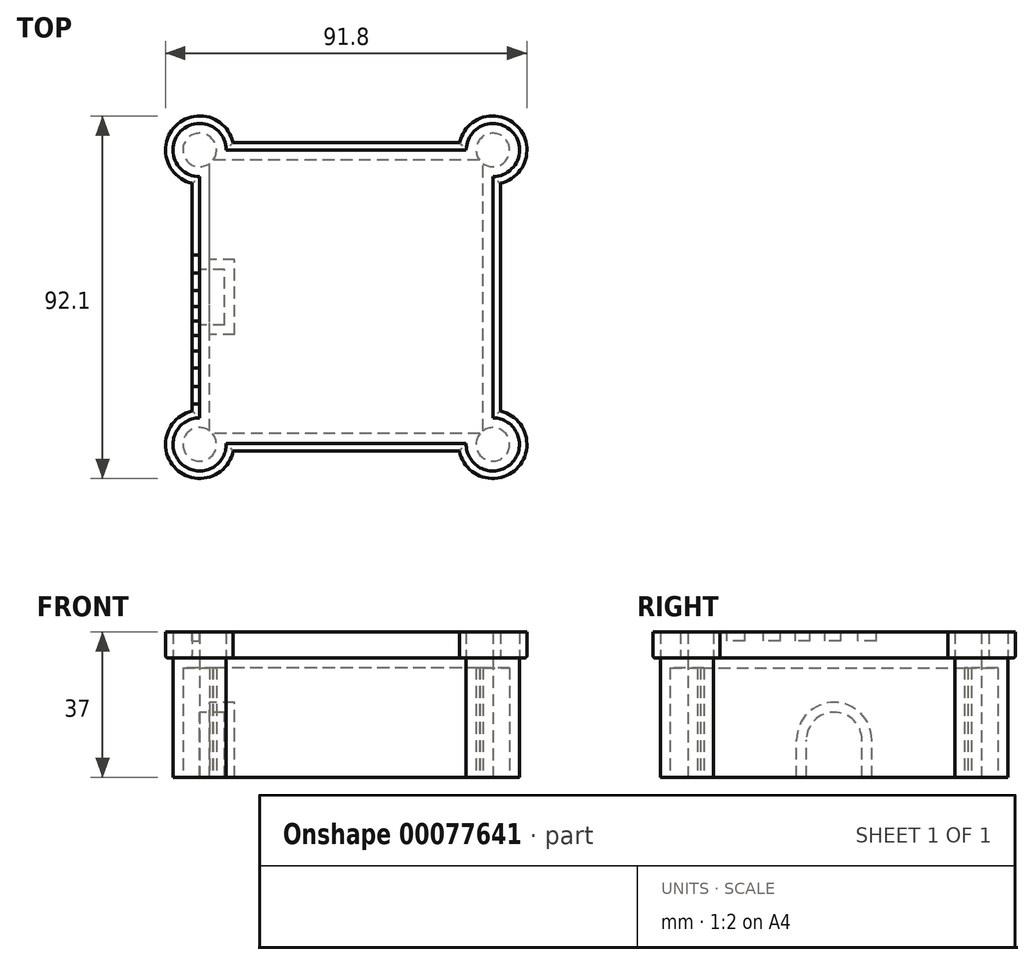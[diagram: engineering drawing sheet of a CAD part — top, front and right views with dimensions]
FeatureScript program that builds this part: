
annotation { "Feature Type Name" : "Feature", "Feature Type Description" : "" }
export const myFeature = defineFeature(function(context is Context, id is Id, definition is map)
    precondition{}
    {
        {
            var Q0;
            Q0=qCreatedBy(makeId("Top.planeOp"),FACE);
            var sketch = newSketch(context, id + "F0", { "sketchPlane" : qUnion([Q0])});
            skLineSegment(sketch, "E0.bottom", {"start": v(37.24, -37.17) * mm, "end": v(-37.24, -37.17) * mm});
            skLineSegment(sketch, "E0.top", {"start": v(37.24, 37.4) * mm, "end": v(-37.24, 37.4) * mm});
            skLineSegment(sketch, "E0.left", {"start": v(37.24, -37.17) * mm, "end": v(37.24, 37.4) * mm});
            skLineSegment(sketch, "E0.right", {"start": v(-37.24, -37.17) * mm, "end": v(-37.24, 37.4) * mm});
            skPoint(sketch, "E0.middle", {"position": v(0, 0.12) * mm});
            skCircle(sketch, "E1", {"center": v(37.24, 37.4) * mm, "radius": 6.76 * mm});
            skCircle(sketch, "E2.MirrorC", {"center": v(37.24, -37.4) * mm, "radius": 6.76 * mm});
            skCircle(sketch, "E3.MirrorC", {"center": v(-37.24, 37.4) * mm, "radius": 6.76 * mm});
            skCircle(sketch, "E4.MirrorC", {"center": v(-37.24, -37.4) * mm, "radius": 6.76 * mm});
            skSolve(sketch);
        }
        {
            var Q0;
            {var subQ5=sQuery(id+"F0.wireOp",EDGE,"E2.MirrorC");var subQ10=sQuery(id+"F0.wireOp",EDGE,"E0.bottom");var subQ11=makeQuery(id+"F0.imprint","INTERSECT",VERTEX,{"derivedFrom":[subQ10,subQ5]});Q0=makeQuery(id+"F0.imprint","IMPRINT",FACE,{"disambiguationData":[TD([[makeQuery(id+"F0.imprint","IMPRINT",EDGE,{"disambiguationData":[TD([[subQ11,-1.0]])],"derivedFrom":subQ10}),-1.0]])]});}
            var Q1;
            {var subQ0=sQuery(id+"F0.wireOp",EDGE,"E0.left");var subQ1=sQuery(id+"F0.wireOp",EDGE,"E0.bottom");var subQ2=makeQuery(id+"F0.imprint","INTERSECT",VERTEX,{"derivedFrom":[subQ1,subQ0]});Q1=makeQuery(id+"F0.imprint","IMPRINT",FACE,{"disambiguationData":[TD([[makeQuery(id+"F0.imprint","IMPRINT",EDGE,{"disambiguationData":[TD([[subQ2,-1.0]])],"derivedFrom":subQ1}),1.0]])]});}
            var Q2;
            {var subQ0=sQuery(id+"F0.wireOp",EDGE,"E0.left");var subQ1=sQuery(id+"F0.wireOp",EDGE,"E0.top");var subQ2=makeQuery(id+"F0.imprint","INTERSECT",VERTEX,{"derivedFrom":[subQ1,subQ0]});Q2=makeQuery(id+"F0.imprint","IMPRINT",FACE,{"disambiguationData":[TD([[makeQuery(id+"F0.imprint","IMPRINT",EDGE,{"disambiguationData":[TD([[subQ2,-1.0]])],"derivedFrom":subQ1}),-1.0]])]});}
            var Q3;
            {var subQ0=sQuery(id+"F0.wireOp",EDGE,"E0.right");var subQ1=sQuery(id+"F0.wireOp",EDGE,"E0.top");var subQ2=makeQuery(id+"F0.imprint","INTERSECT",VERTEX,{"derivedFrom":[subQ1,subQ0]});Q3=makeQuery(id+"F0.imprint","IMPRINT",FACE,{"disambiguationData":[TD([[makeQuery(id+"F0.imprint","IMPRINT",EDGE,{"disambiguationData":[TD([[subQ2,1.0]])],"derivedFrom":subQ1}),-1.0]])]});}
            var Q4;
            {var subQ0=sQuery(id+"F0.wireOp",EDGE,"E0.right");var subQ1=sQuery(id+"F0.wireOp",EDGE,"E0.bottom");var subQ2=makeQuery(id+"F0.imprint","INTERSECT",VERTEX,{"derivedFrom":[subQ1,subQ0]});Q4=makeQuery(id+"F0.imprint","IMPRINT",FACE,{"disambiguationData":[TD([[makeQuery(id+"F0.imprint","IMPRINT",EDGE,{"disambiguationData":[TD([[subQ2,1.0]])],"derivedFrom":subQ1}),1.0]])]});}
            var Q5;
            {var subQ0=sQuery(id+"F0.wireOp",EDGE,"E0.right");var subQ1=sQuery(id+"F0.wireOp",EDGE,"E0.bottom");var subQ2=makeQuery(id+"F0.imprint","INTERSECT",VERTEX,{"derivedFrom":[subQ1,subQ0]});Q5=makeQuery(id+"F0.imprint","IMPRINT",FACE,{"disambiguationData":[TD([[makeQuery(id+"F0.imprint","IMPRINT",EDGE,{"disambiguationData":[TD([[subQ2,1.0]])],"derivedFrom":subQ1}),-1.0]])]});}
            var Q6;
            {var subQ0=sQuery(id+"F0.wireOp",EDGE,"E0.right");var subQ1=sQuery(id+"F0.wireOp",EDGE,"E0.top");var subQ2=makeQuery(id+"F0.imprint","INTERSECT",VERTEX,{"derivedFrom":[subQ1,subQ0]});Q6=makeQuery(id+"F0.imprint","IMPRINT",FACE,{"disambiguationData":[TD([[makeQuery(id+"F0.imprint","IMPRINT",EDGE,{"disambiguationData":[TD([[subQ2,1.0]])],"derivedFrom":subQ1}),1.0]])]});}
            var Q7;
            {var subQ0=sQuery(id+"F0.wireOp",EDGE,"E0.left");var subQ1=sQuery(id+"F0.wireOp",EDGE,"E0.top");var subQ2=makeQuery(id+"F0.imprint","INTERSECT",VERTEX,{"derivedFrom":[subQ1,subQ0]});Q7=makeQuery(id+"F0.imprint","IMPRINT",FACE,{"disambiguationData":[TD([[makeQuery(id+"F0.imprint","IMPRINT",EDGE,{"disambiguationData":[TD([[subQ2,-1.0]])],"derivedFrom":subQ1}),1.0]])]});}
            var Q8;
            {var subQ0=sQuery(id+"F0.wireOp",EDGE,"E0.left");var subQ1=sQuery(id+"F0.wireOp",EDGE,"E0.bottom");var subQ2=makeQuery(id+"F0.imprint","INTERSECT",VERTEX,{"derivedFrom":[subQ1,subQ0]});Q8=makeQuery(id+"F0.imprint","IMPRINT",FACE,{"disambiguationData":[TD([[makeQuery(id+"F0.imprint","IMPRINT",EDGE,{"disambiguationData":[TD([[subQ2,-1.0]])],"derivedFrom":subQ1}),-1.0]])]});}
            extrude(context, id + "F1", {"entities" : qUnion([Q0, Q1, Q2, Q3, Q4, Q5, Q6, Q7, Q8]), "depth" : 30.38 * mm});
        }
        {
            var Q0;
            Q0=makeQuery(id+"F1.opExtrude","CAP_FACE",FACE,{"disambiguationData":[OSD([sQuery(id+"F0.wireOp",EDGE,"E0.bottom"),sQuery(id+"F0.wireOp",EDGE,"E0.top"),sQuery(id+"F0.wireOp",EDGE,"E0.left"),sQuery(id+"F0.wireOp",EDGE,"E0.right"),sQuery(id+"F0.wireOp",EDGE,"E1"),sQuery(id+"F0.wireOp",EDGE,"E2.MirrorC"),sQuery(id+"F0.wireOp",EDGE,"E3.MirrorC"),sQuery(id+"F0.wireOp",EDGE,"E4.MirrorC")])],"isStart":false});
            var sketch = newSketch(context, id + "F2", { "sketchPlane" : qUnion([Q0])});
            skArc(sketch, "E5.0", {"start": v(-39.14, -28.95) * mm, "mid": v(-43.28, -43.6) * mm, "end": v(-28.75, -39.06) * mm});
            skLineSegment(sketch, "E5.1", {"start": v(-39.14, 28.95) * mm, "end": v(-39.14, -28.95) * mm});
            skLineSegment(sketch, "E5.2", {"start": v(-28.75, -39.06) * mm, "end": v(28.75, -39.06) * mm});
            skArc(sketch, "E5.3", {"start": v(-28.8, 39.3) * mm, "mid": v(-43.37, 43.52) * mm, "end": v(-39.14, 28.95) * mm});
            skArc(sketch, "E5.4", {"start": v(28.75, -39.06) * mm, "mid": v(43.28, -43.6) * mm, "end": v(39.14, -28.95) * mm});
            skLineSegment(sketch, "E5.5", {"start": v(39.14, -28.95) * mm, "end": v(39.14, 28.95) * mm});
            skArc(sketch, "E5.6", {"start": v(39.14, 28.95) * mm, "mid": v(43.37, 43.52) * mm, "end": v(28.8, 39.3) * mm});
            skLineSegment(sketch, "E5.7", {"start": v(28.8, 39.3) * mm, "end": v(-28.8, 39.3) * mm});
            skSolve(sketch);
        }
        {
            var Q0;
            Q0=makeQuery(id+"F2.imprint","IMPRINT",FACE,{"disambiguationData":[TD([[makeQuery(id+"F2.imprint","IMPRINT",EDGE,{"derivedFrom":sQuery(id+"F2.wireOp",EDGE,"E5.0")}),1.0]])]});
            extrude(context, id + "F3", {"entities" : qUnion([Q0]), "depth" : 6.62 * mm});
        }
        {
            var Q0;
            Q0=makeQuery(id+"F3.opExtrude","CAP_FACE",FACE,{"disambiguationData":[OSD([sQuery(id+"F0.wireOp",EDGE,"E0.bottom"),sQuery(id+"F0.wireOp",EDGE,"E0.top"),sQuery(id+"F0.wireOp",EDGE,"E0.left"),sQuery(id+"F0.wireOp",EDGE,"E0.right"),sQuery(id+"F0.wireOp",EDGE,"E1"),sQuery(id+"F0.wireOp",EDGE,"E2.MirrorC"),sQuery(id+"F0.wireOp",EDGE,"E3.MirrorC"),sQuery(id+"F0.wireOp",EDGE,"E4.MirrorC"),sQuery(id+"F2.wireOp",EDGE,"E5.0"),sQuery(id+"F2.wireOp",EDGE,"E5.1"),sQuery(id+"F2.wireOp",EDGE,"E5.2"),sQuery(id+"F2.wireOp",EDGE,"E5.3"),sQuery(id+"F2.wireOp",EDGE,"E5.4"),sQuery(id+"F2.wireOp",EDGE,"E5.5"),sQuery(id+"F2.wireOp",EDGE,"E5.6"),sQuery(id+"F2.wireOp",EDGE,"E5.7")])],"isStart":false});
            var sketch = newSketch(context, id + "F4", { "sketchPlane" : qUnion([Q0])});
            skLineSegment(sketch, "E6", {"start": v(-39.14, -27.2) * mm, "end": v(-37.24, -27.2) * mm});
            skLineSegment(sketch, "E7", {"start": v(-37.24, -27.2) * mm, "end": v(-37.24, -22.66) * mm});
            skLineSegment(sketch, "E8", {"start": v(-37.24, -22.66) * mm, "end": v(-39.14, -22.66) * mm});
            skLineSegment(sketch, "E9", {"start": v(-39.14, -22.66) * mm, "end": v(-39.14, -18) * mm});
            skLineSegment(sketch, "E10", {"start": v(-39.14, -18) * mm, "end": v(-37.24, -18) * mm});
            skLineSegment(sketch, "E11", {"start": v(-37.24, -18) * mm, "end": v(-37.24, -13.7) * mm});
            skLineSegment(sketch, "E12", {"start": v(-37.24, -13.7) * mm, "end": v(-39.14, -13.7) * mm});
            skLineSegment(sketch, "E13", {"start": v(-39.14, -13.7) * mm, "end": v(-39.14, -9.78) * mm});
            skLineSegment(sketch, "E14", {"start": v(-39.14, -9.78) * mm, "end": v(-37.24, -9.78) * mm});
            skLineSegment(sketch, "E15", {"start": v(-37.24, -9.78) * mm, "end": v(-37.24, -6.1) * mm});
            skLineSegment(sketch, "E16", {"start": v(-37.24, -6.1) * mm, "end": v(-39.14, -6.1) * mm});
            skLineSegment(sketch, "E17", {"start": v(-39.14, -6.1) * mm, "end": v(-39.14, -2.36) * mm});
            skLineSegment(sketch, "E18", {"start": v(-39.14, -2.36) * mm, "end": v(-37.24, -2.36) * mm});
            skLineSegment(sketch, "E19", {"start": v(-37.24, -2.36) * mm, "end": v(-37.24, 1.72) * mm});
            skLineSegment(sketch, "E20", {"start": v(-37.24, 1.72) * mm, "end": v(-39.14, 1.72) * mm});
            skLineSegment(sketch, "E21", {"start": v(-39.14, 1.72) * mm, "end": v(-39.14, 6.1) * mm});
            skLineSegment(sketch, "E22", {"start": v(-39.14, 6.1) * mm, "end": v(-37.24, 6.1) * mm});
            skLineSegment(sketch, "E23", {"start": v(-37.24, 6.1) * mm, "end": v(-37.24, 10.7) * mm});
            skLineSegment(sketch, "E24", {"start": v(-37.24, 10.7) * mm, "end": v(-39.14, 10.7) * mm});
            skSolve(sketch);
        }
        {
            var Q0;
            {var subQ0=sQuery(id+"F4.wireOp",EDGE,"E6");Q0=makeQuery(id+"F4.imprint","IMPRINT",FACE,{"disambiguationData":[TD([[makeQuery(id+"F4.imprint","IMPRINT",EDGE,{"derivedFrom":subQ0}),1.0]])]});}
            var Q1;
            {var subQ0=sQuery(id+"F4.wireOp",EDGE,"E10");Q1=makeQuery(id+"F4.imprint","IMPRINT",FACE,{"disambiguationData":[TD([[makeQuery(id+"F4.imprint","IMPRINT",EDGE,{"derivedFrom":subQ0}),1.0]])]});}
            var Q2;
            {var subQ0=sQuery(id+"F4.wireOp",EDGE,"E14");Q2=makeQuery(id+"F4.imprint","IMPRINT",FACE,{"disambiguationData":[TD([[makeQuery(id+"F4.imprint","IMPRINT",EDGE,{"derivedFrom":subQ0}),1.0]])]});}
            var Q3;
            {var subQ0=sQuery(id+"F4.wireOp",EDGE,"E18");Q3=makeQuery(id+"F4.imprint","IMPRINT",FACE,{"disambiguationData":[TD([[makeQuery(id+"F4.imprint","IMPRINT",EDGE,{"derivedFrom":subQ0}),1.0]])]});}
            var Q4;
            {var subQ0=sQuery(id+"F4.wireOp",EDGE,"E22");Q4=makeQuery(id+"F4.imprint","IMPRINT",FACE,{"disambiguationData":[TD([[makeQuery(id+"F4.imprint","IMPRINT",EDGE,{"derivedFrom":subQ0}),1.0]])]});}
            extrude(context, id + "F5", {"entities" : qUnion([Q0, Q1, Q2, Q3, Q4]), "operationType" : NewBodyOperationType.REMOVE, "oppositeDirection" : true, "depth" : 2.25 * mm});
        }
        {
            var Q0;
            Q0=makeQuery(id+"F3.opExtrude","CAP_EDGE",EDGE,{"disambiguationData":[OSD([sQuery(id+"F2.wireOp",EDGE,"E5.4")])],"isStart":true});
            var Q1;
            Q1=makeQuery(id+"F3.opExtrude","CAP_EDGE",EDGE,{"disambiguationData":[OSD([sQuery(id+"F2.wireOp",EDGE,"E5.2")])],"isStart":true});
            var Q2;
            Q2=makeQuery(id+"F3.opExtrude","CAP_EDGE",EDGE,{"disambiguationData":[OSD([sQuery(id+"F2.wireOp",EDGE,"E5.0")])],"isStart":true});
            var Q3;
            Q3=makeQuery(id+"F3.opExtrude","CAP_EDGE",EDGE,{"disambiguationData":[OSD([sQuery(id+"F2.wireOp",EDGE,"E5.1")])],"isStart":true});
            var Q4;
            Q4=makeQuery(id+"F3.opExtrude","CAP_EDGE",EDGE,{"disambiguationData":[OSD([sQuery(id+"F2.wireOp",EDGE,"E5.3")])],"isStart":true});
            var Q5;
            Q5=makeQuery(id+"F3.opExtrude","CAP_EDGE",EDGE,{"disambiguationData":[OSD([sQuery(id+"F2.wireOp",EDGE,"E5.7")])],"isStart":true});
            var Q6;
            Q6=makeQuery(id+"F3.opExtrude","CAP_EDGE",EDGE,{"disambiguationData":[OSD([sQuery(id+"F2.wireOp",EDGE,"E5.6")])],"isStart":true});
            var Q7;
            Q7=makeQuery(id+"F3.opExtrude","CAP_EDGE",EDGE,{"disambiguationData":[OSD([sQuery(id+"F2.wireOp",EDGE,"E5.5")])],"isStart":true});
            fillet(context, id + "F6", {"entities" : qUnion([Q0, Q1, Q2, Q3, Q4, Q5, Q6, Q7]), "radius" : 0.72 * mm, "tangentPropagation" : true, "rho" : 0.5, "crossSection" : FilletCrossSection.CONIC, "allowEdgeOverflow" : false});
        }
        {
            var Q0;
            Q0=makeQuery(id+"F1.opExtrude","SWEPT_FACE",FACE,{"disambiguationData":[OSD([sQuery(id+"F0.wireOp",EDGE,"E0.right")])]});
            var sketch = newSketch(context, id + "F7", { "sketchPlane" : qUnion([Q0])});
            skLineSegment(sketch, "E25.bottom", {"start": v(-7.05, 0) * mm, "end": v(7.05, 0) * mm});
            skLineSegment(sketch, "E25.top", {"start": v(-7.05, 9.56) * mm, "end": v(7.05, 9.56) * mm});
            skLineSegment(sketch, "E25.left", {"start": v(-7.05, 0) * mm, "end": v(-7.05, 9.56) * mm});
            skLineSegment(sketch, "E25.right", {"start": v(7.05, 0) * mm, "end": v(7.05, 9.56) * mm});
            skArc(sketch, "E26", {"start": v(7.05, 9.56) * mm, "mid": v(0, 16.6) * mm, "end": v(-7.05, 9.56) * mm});
            skSolve(sketch);
        }
        {
            var Q0;
            Q0=makeQuery(id+"F7.imprint","IMPRINT",FACE,{"disambiguationData":[TD([[makeQuery(id+"F7.imprint","IMPRINT",EDGE,{"derivedFrom":sQuery(id+"F7.wireOp",EDGE,"E25.bottom")}),-1.0]])]});
            var Q1;
            Q1=makeQuery(id+"F7.imprint","IMPRINT",FACE,{"disambiguationData":[TD([[makeQuery(id+"F7.imprint","IMPRINT",EDGE,{"derivedFrom":sQuery(id+"F7.wireOp",EDGE,"E25.top")}),1.0]])]});
            extrude(context, id + "F8", {"entities" : qUnion([Q0, Q1]), "operationType" : NewBodyOperationType.REMOVE, "endBound" : BoundingType.SYMMETRIC, "oppositeDirection" : true, "depth" : 12.8 * mm});
        }
        {
            var Q0;
            Q0=makeQuery(id+"F1.opExtrude","CAP_FACE",FACE,{"disambiguationData":[OSD([sQuery(id+"F0.wireOp",EDGE,"E0.bottom"),sQuery(id+"F0.wireOp",EDGE,"E0.top"),sQuery(id+"F0.wireOp",EDGE,"E0.left"),sQuery(id+"F0.wireOp",EDGE,"E0.right"),sQuery(id+"F0.wireOp",EDGE,"E1"),sQuery(id+"F0.wireOp",EDGE,"E2.MirrorC"),sQuery(id+"F0.wireOp",EDGE,"E3.MirrorC"),sQuery(id+"F0.wireOp",EDGE,"E4.MirrorC")])],"isStart":true});
            shell(context, id + "F9", {"entities" : qUnion([Q0]), "thickness" : 2.5 * mm});
        }
    });
